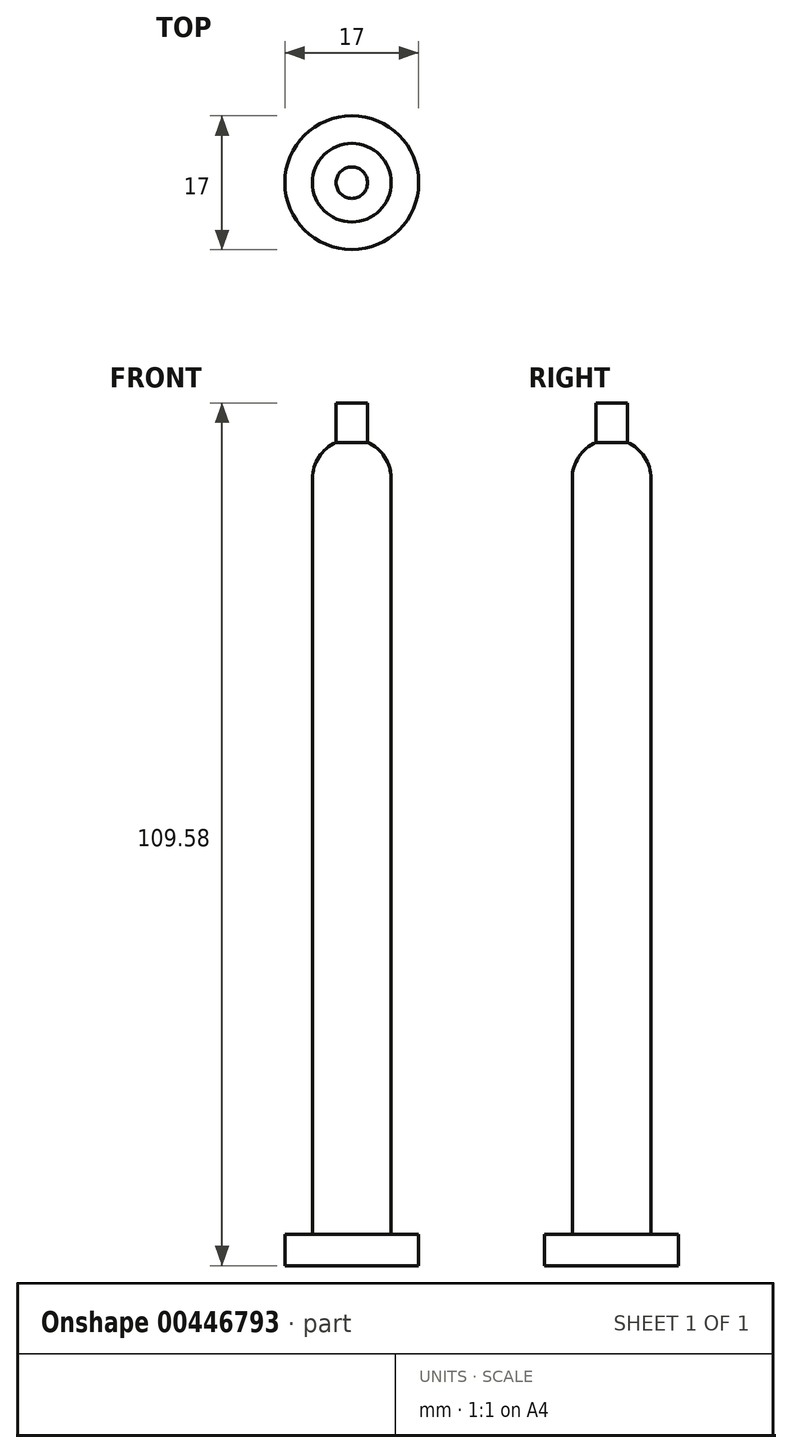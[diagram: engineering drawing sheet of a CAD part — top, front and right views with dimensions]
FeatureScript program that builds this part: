
annotation { "Feature Type Name" : "Feature", "Feature Type Description" : "" }
export const myFeature = defineFeature(function(context is Context, id is Id, definition is map)
    precondition{}
    {
        {
            var Q0;
            Q0=qCreatedBy(makeId("Top.planeOp"),FACE);
            var sketch = newSketch(context, id + "F0", { "sketchPlane" : qUnion([Q0])});
            skCircle(sketch, "E0", {"center": v(0, 0) * mm, "radius": 8.5 * mm});
            skSolve(sketch);
        }
        {
            var Q0;
            Q0=qSketchRegion(id+"F0",true);
            extrude(context, id + "F1", {"entities" : qUnion([Q0]), "depth" : 4 * mm});
        }
        {
            var Q0;
            Q0=qCreatedBy(makeId("Top.planeOp"),FACE);
            var sketch = newSketch(context, id + "F2", { "sketchPlane" : qUnion([Q0])});
            skCircle(sketch, "E1", {"center": v(0, 0) * mm, "radius": 5 * mm});
            skSolve(sketch);
        }
        {
            var Q0;
            Q0=qSketchRegion(id+"F2",true);
            extrude(context, id + "F3", {"entities" : qUnion([Q0]), "operationType" : NewBodyOperationType.ADD, "depth" : 100 * mm});
        }
        {
            var Q0;
            Q0=qCreatedBy(makeId("Right.planeOp"),FACE);
            var sketch = newSketch(context, id + "F4", { "sketchPlane" : qUnion([Q0])});
            skLineSegment(sketch, "E2", {"start": v(0, 100) * mm, "end": v(5, 100) * mm});
            skArc(sketch, "E3", {"start": v(5, 100) * mm, "mid": v(3.54, 103.54) * mm, "end": v(0, 105) * mm});
            skLineSegment(sketch, "E4", {"start": v(0, 109.58) * mm, "end": v(2, 109.58) * mm});
            skLineSegment(sketch, "E5", {"start": v(2, 109.58) * mm, "end": v(2, 104.58) * mm});
            skLineSegment(sketch, "E6", {"start": v(2, 104.58) * mm, "end": v(0, 104.58) * mm});
            skLineSegment(sketch, "E7", {"start": v(0, 109.58) * mm, "end": v(0, 100) * mm});
            skSolve(sketch);
        }
        {
            var Q0;
            {var subQ0=sQuery(id+"F4.wireOp",EDGE,"E2");Q0=makeQuery(id+"F4.imprint","IMPRINT",FACE,{"disambiguationData":[TD([[makeQuery(id+"F4.imprint","IMPRINT",EDGE,{"derivedFrom":subQ0}),1.0]])]});}
            var Q1;
            {var subQ4=sQuery(id+"F4.wireOp",EDGE,"E4");Q1=makeQuery(id+"F4.imprint","IMPRINT",FACE,{"disambiguationData":[TD([[makeQuery(id+"F4.imprint","IMPRINT",EDGE,{"derivedFrom":subQ4}),-1.0]])]});}
            var Q2;
            {var subQ3=sQuery(id+"F4.wireOp",EDGE,"E6");Q2=makeQuery(id+"F4.imprint","IMPRINT",FACE,{"disambiguationData":[TD([[makeQuery(id+"F4.imprint","IMPRINT",EDGE,{"derivedFrom":subQ3}),-1.0]])]});}
            var Q3;
            Q3=sQuery(id+"F4.wireOp",EDGE,"E7");
            revolve(context, id + "F5", {"operationType" : NewBodyOperationType.ADD, "entities" : qUnion([Q0, Q1, Q2]), "axis" : qUnion([Q3]), "revolveType" : RevolveType.FULL});
        }
    });
